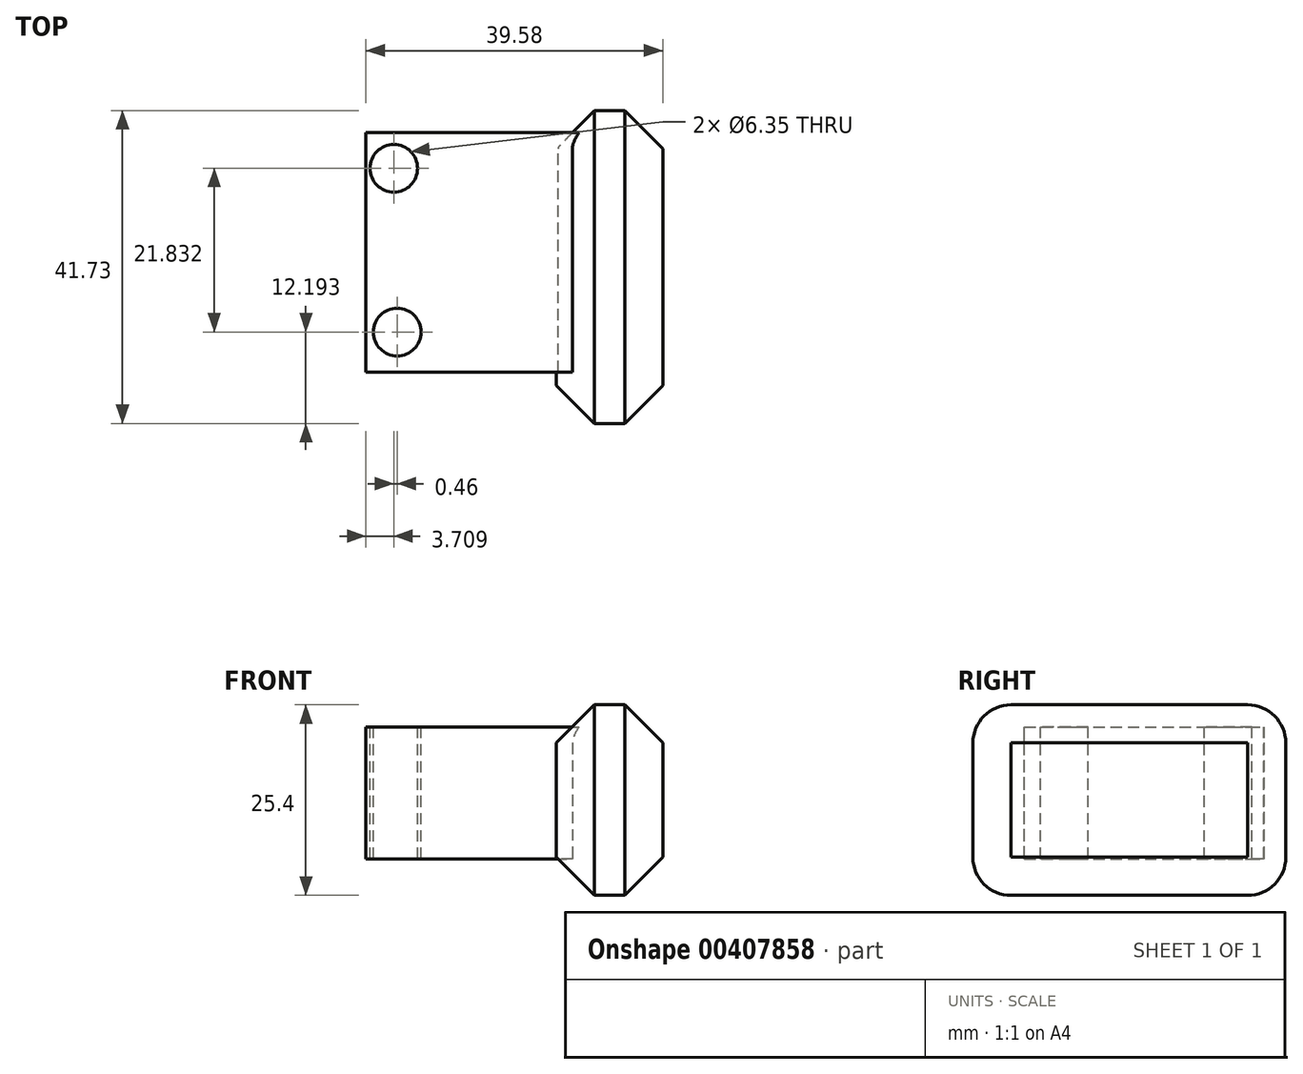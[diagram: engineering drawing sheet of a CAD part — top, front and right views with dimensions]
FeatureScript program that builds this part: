
annotation { "Feature Type Name" : "Feature", "Feature Type Description" : "" }
export const myFeature = defineFeature(function(context is Context, id is Id, definition is map)
    precondition{}
    {
        {
            var Q0;
            Q0=qCreatedBy(makeId("Top.planeOp"),FACE);
            var sketch = newSketch(context, id + "F0", { "sketchPlane" : qUnion([Q0])});
            skLineSegment(sketch, "E0.bottom", {"start": v(-50.39, 0) * mm, "end": v(-36.21, 0) * mm});
            skLineSegment(sketch, "E0.top", {"start": v(-50.39, -41.73) * mm, "end": v(-36.21, -41.73) * mm});
            skLineSegment(sketch, "E0.left", {"start": v(-50.39, 0) * mm, "end": v(-50.39, -41.73) * mm});
            skLineSegment(sketch, "E0.right", {"start": v(-36.21, 0) * mm, "end": v(-36.21, -41.73) * mm});
            skSolve(sketch);
        }
        {
            var Q0;
            Q0=makeQuery(id+"F0.imprint","IMPRINT",FACE,{"disambiguationData":[TD([[makeQuery(id+"F0.imprint","IMPRINT",EDGE,{"derivedFrom":sQuery(id+"F0.wireOp",EDGE,"E0.bottom")}),-1.0]])]});
            extrude(context, id + "F1", {"entities" : qUnion([Q0]), "depth" : 25.4 * mm, "offsetDistance" : 25.4 * mm});
        }
        {
            var Q0;
            Q0=makeQuery(id+"F1.opExtrude","CAP_EDGE",EDGE,{"disambiguationData":[OSD([sQuery(id+"F0.wireOp",EDGE,"E0.top")])],"isStart":false});
            fillet(context, id + "F2", {"entities" : qUnion([Q0]), "tangentPropagation" : true, "radius" : 5.08 * mm, "defaultsChanged" : false, "vertexSettings" : [], "allowEdgeOverflow" : false});
        }
        {
            var Q0;
            Q0=makeQuery(id+"F1.opExtrude","CAP_EDGE",EDGE,{"disambiguationData":[OSD([sQuery(id+"F0.wireOp",EDGE,"E0.top")])],"isStart":true});
            fillet(context, id + "F3", {"entities" : qUnion([Q0]), "tangentPropagation" : true, "radius" : 5.08 * mm, "defaultsChanged" : false, "vertexSettings" : [], "allowEdgeOverflow" : false});
        }
        {
            var Q0;
            Q0=makeQuery(id+"F1.opExtrude","CAP_EDGE",EDGE,{"disambiguationData":[OSD([sQuery(id+"F0.wireOp",EDGE,"E0.bottom")])],"isStart":true});
            fillet(context, id + "F4", {"entities" : qUnion([Q0]), "tangentPropagation" : true, "radius" : 5.08 * mm, "defaultsChanged" : false, "vertexSettings" : [], "allowEdgeOverflow" : false});
        }
        {
            var Q0;
            Q0=makeQuery(id+"F1.opExtrude","CAP_EDGE",EDGE,{"disambiguationData":[OSD([sQuery(id+"F0.wireOp",EDGE,"E0.bottom")])],"isStart":false});
            fillet(context, id + "F5", {"entities" : qUnion([Q0]), "tangentPropagation" : true, "radius" : 5.08 * mm, "defaultsChanged" : false, "vertexSettings" : [], "allowEdgeOverflow" : false});
        }
        {
            var Q0;
            Q0=makeQuery(id+"F1.opExtrude","SWEPT_FACE",FACE,{"disambiguationData":[OSD([sQuery(id+"F0.wireOp",EDGE,"E0.left")])]});
            var sketch = newSketch(context, id + "F6", { "sketchPlane" : qUnion([Q0])});
            skLineSegment(sketch, "E1.bottom", {"start": v(34.85, 4.88) * mm, "end": v(2.94, 4.88) * mm});
            skLineSegment(sketch, "E1.top", {"start": v(34.85, 22.46) * mm, "end": v(2.94, 22.46) * mm});
            skLineSegment(sketch, "E1.left", {"start": v(34.85, 4.88) * mm, "end": v(34.85, 22.46) * mm});
            skLineSegment(sketch, "E1.right", {"start": v(2.94, 4.88) * mm, "end": v(2.94, 22.46) * mm});
            skSolve(sketch);
        }
        {
            var Q0;
            Q0=makeQuery(id+"F1.opExtrude","SWEPT_FACE",FACE,{"disambiguationData":[OSD([sQuery(id+"F0.wireOp",EDGE,"E0.left")])]});
            var Q1;
            Q1=makeQuery(id+"F6.imprint","IMPRINT",FACE,{"disambiguationData":[TD([[makeQuery(id+"F6.imprint","IMPRINT",EDGE,{"derivedFrom":sQuery(id+"F6.wireOp",EDGE,"E1.bottom")}),-1.0]])]});
            extrude(context, id + "F7", {"entities" : qUnion([Q0, Q1]), "operationType" : NewBodyOperationType.ADD, "oppositeDirection" : true, "depth" : 12.7 * mm, "offsetDistance" : 25.4 * mm});
        }
        {
            var Q0;
            Q0=makeQuery(id+"F6.imprint","IMPRINT",FACE,{"disambiguationData":[TD([[makeQuery(id+"F6.imprint","IMPRINT",EDGE,{"derivedFrom":sQuery(id+"F6.wireOp",EDGE,"E1.bottom")}),-1.0]])]});
            extrude(context, id + "F8", {"entities" : qUnion([Q0]), "operationType" : NewBodyOperationType.ADD, "depth" : 25.4 * mm, "offsetDistance" : 25.4 * mm});
        }
        {
            var Q0;
            Q0=makeQuery(id+"F8.opExtrude","SWEPT_FACE",FACE,{"disambiguationData":[OSD([sQuery(id+"F6.wireOp",EDGE,"E1.top")])]});
            var sketch = newSketch(context, id + "F9", { "sketchPlane" : qUnion([Q0])});
            skCircle(sketch, "E2", {"center": v(-72.08, -7.7) * mm, "radius": 2.7 * mm});
            skCircle(sketch, "E3", {"center": v(-71.62, -29.54) * mm, "radius": 3.37 * mm});
            skSolve(sketch);
        }
        {
            var Q0;
            Q0=sQuery(id+"F9.wireOp",VERTEX,"E3.center");
            var Q1;
            Q1=makeQuery(id+"F1.opExtrude","SWEPT_BODY",BODY,{"disambiguationData":[OSD([sQuery(id+"F0.wireOp",EDGE,"E0.bottom"),sQuery(id+"F0.wireOp",EDGE,"E0.top"),sQuery(id+"F0.wireOp",EDGE,"E0.left"),sQuery(id+"F0.wireOp",EDGE,"E0.right")])]});
            hole(context, id + "F10", {"style" : HoleStyle.SIMPLE, "endStyle" : HoleEndStyle.THROUGH, "holeDiameter" : 6.35 * mm, "majorDiameter" : 6.35 * mm, "isTappedThrough" : true, "tappedDepth" : 12.7 * mm, "tapClearance" : 3, "locations" : qUnion([Q0]), "scope" : qUnion([Q1])});
        }
        {
            var Q0;
            Q0=sQuery(id+"F9.wireOp",VERTEX,"E2.center");
            var Q1;
            Q1=makeQuery(id+"F1.opExtrude","SWEPT_BODY",BODY,{"disambiguationData":[OSD([sQuery(id+"F0.wireOp",EDGE,"E0.bottom"),sQuery(id+"F0.wireOp",EDGE,"E0.top"),sQuery(id+"F0.wireOp",EDGE,"E0.left"),sQuery(id+"F0.wireOp",EDGE,"E0.right")])]});
            hole(context, id + "F11", {"style" : HoleStyle.SIMPLE, "endStyle" : HoleEndStyle.THROUGH, "holeDiameter" : 6.35 * mm, "majorDiameter" : 6.35 * mm, "isTappedThrough" : true, "tappedDepth" : 12.7 * mm, "tapClearance" : 3, "locations" : qUnion([Q0]), "scope" : qUnion([Q1])});
        }
        {
            var Q0;
            Q0=makeQuery(id+"F2.opFillet","BLEND_FACE",FACE,{"disambiguationData":[OSD([sQuery(id+"F0.wireOp",EDGE,"E0.top")])]});
            chamfer(context, id + "F12", {"entities" : qUnion([Q0]), "width" : 5.08 * mm, "tangentPropagation" : true});
        }
    });
